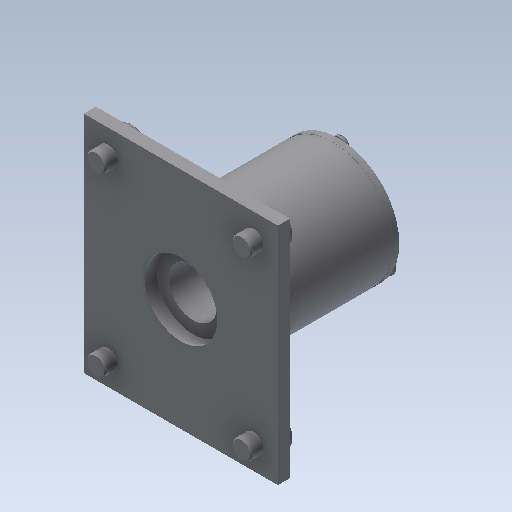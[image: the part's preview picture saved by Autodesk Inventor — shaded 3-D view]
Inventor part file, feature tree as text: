
AUTODESK INVENTOR PART (.ipt)
format: ipt  version: 2021 (Build 250183000, 183)  size: 376,320 bytes
history: native  units: in
note: dims shown in document units (in); Inventor stores cm internally (conversion verified against a paired STEP export)
features: sketch x8, extrude x7, other x6, revolve x1, plane x1, fillet x1, chamfer x1
ambient origin geometry x8: Origin, YZ Plane, XZ Plane, XY Plane, X Axis, Y Axis, Z Axis, Center Point
bodies: Solid1 (feature_tree)
feature tree (25):
  revolve  "Revolution1"  [1 undecoded]
  extrude  "Extrusion7"  Depth=0.122in
  plane  "Work Plane3"
  extrude  "Extrusion6"  Depth=1.0in
  extrude  "Extrusion1"  Depth=3.25in
  extrude  "Extrusion2"  Depth=0.25in
  fillet  "Fillet1"  Radius=0.085in
  extrude  "Extrusion3"  Depth=0.09in
  extrude  "Extrusion4"  Depth=0.01in
  extrude  "Extrusion5"  Depth=0.3in
  chamfer  "Chamfer1"  Distance=2.0in
  other  "WP_J+H-L1"
  other  "WP_J+H-L2"
  other  "WP_J+H-L3"
  other  "Centre1"
  other  "WP_Housing-REAR"
  other  "WP_H"
  sketch  "Sketch1"  dims[d1=0.75in d2=1.25in d3=0.5in]
  sketch  "Sketch2"  dims[d4=0.064in d5=0.122in]
  sketch  "Sketch3"  dims[d6=0.377in d7=1.0in]
  sketch  "Sketch4"  dims[d8=0.125in d9=3.25in]
  sketch  "Sketch5"  dims[d10=0.25in d12=0.625in d13=0.085in]
  sketch  "Sketch6"  dims[d14=0.09in d15=0.075in]
  sketch  "Sketch7"  dims[d17=1.25in d20=0.01in]
  sketch  "Sketch8"  dims[d24=90.0deg d25=0.6871in d27=2.0in d28=0.6871in d29=0.322in d30=1.115in d31=1.115in d32=120.0deg d33=120.0deg d34=0.096in d35=0.0in d36=0.054in d37=0.5in d38=0.25in d39=0.054in d40=0.5in d42=0.054in d43=0.5in d45=0.058in d46=0.0in d47=0.052in d48=0.25in d49=0.25in d51=0.65in d54=0.25in d55=0.0in d56=0.3in d57=0.3in d58=0.3in d59=0.16in d60=0.0in d61=0.4in d62=0.25in d63=0.0in d64=0.025in d65=0.125in d66=45.0deg d69=0.234in d70=0.688in d72=0.218in d74=0.5in d75=0.0in d77=4.63in d78=4.0in d79=3.0in d80=3.625in d81=0.344in d82=0.25in d83=0.0in d84=0.688in d85=2.125in d86=0.3in d87=0.0in d88=0.0in]
note: 1 required parameter value undecoded (feature->parameter linkage not recoverable at this tier; creation-order binding heuristic only, values carry confidence <= 0.55)
